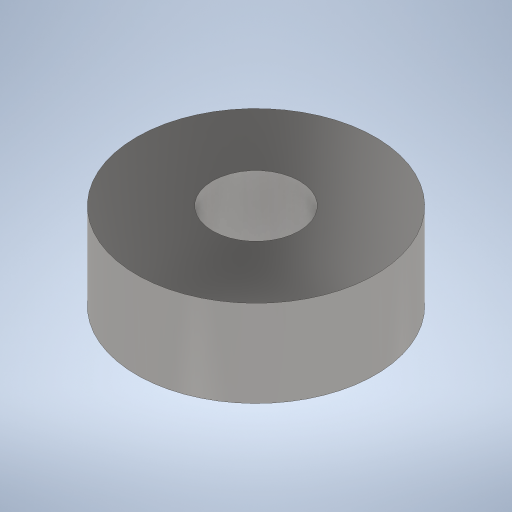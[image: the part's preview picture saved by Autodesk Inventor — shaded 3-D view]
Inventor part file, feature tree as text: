
AUTODESK INVENTOR PART (.ipt)
format: ipt  version: 2024 (Build 280153000, 153)  size: 222,208 bytes
history: native  units: in
note: dims shown in document units (in); Inventor stores cm internally (conversion verified against a paired STEP export)
features: extrude x1, sketch x1
ambient origin geometry x8: Origin, YZ Plane, XZ Plane, XY Plane, X Axis, Y Axis, Z Axis, Center Point
bodies: Solid1 (feature_tree)
feature tree (2):
  extrude  "Extrusion1"  Depth=0.25in
  sketch  "Sketch1"  dims[d0=0.6875in d1=0.25in d2=0.25in d3=0.0in]
